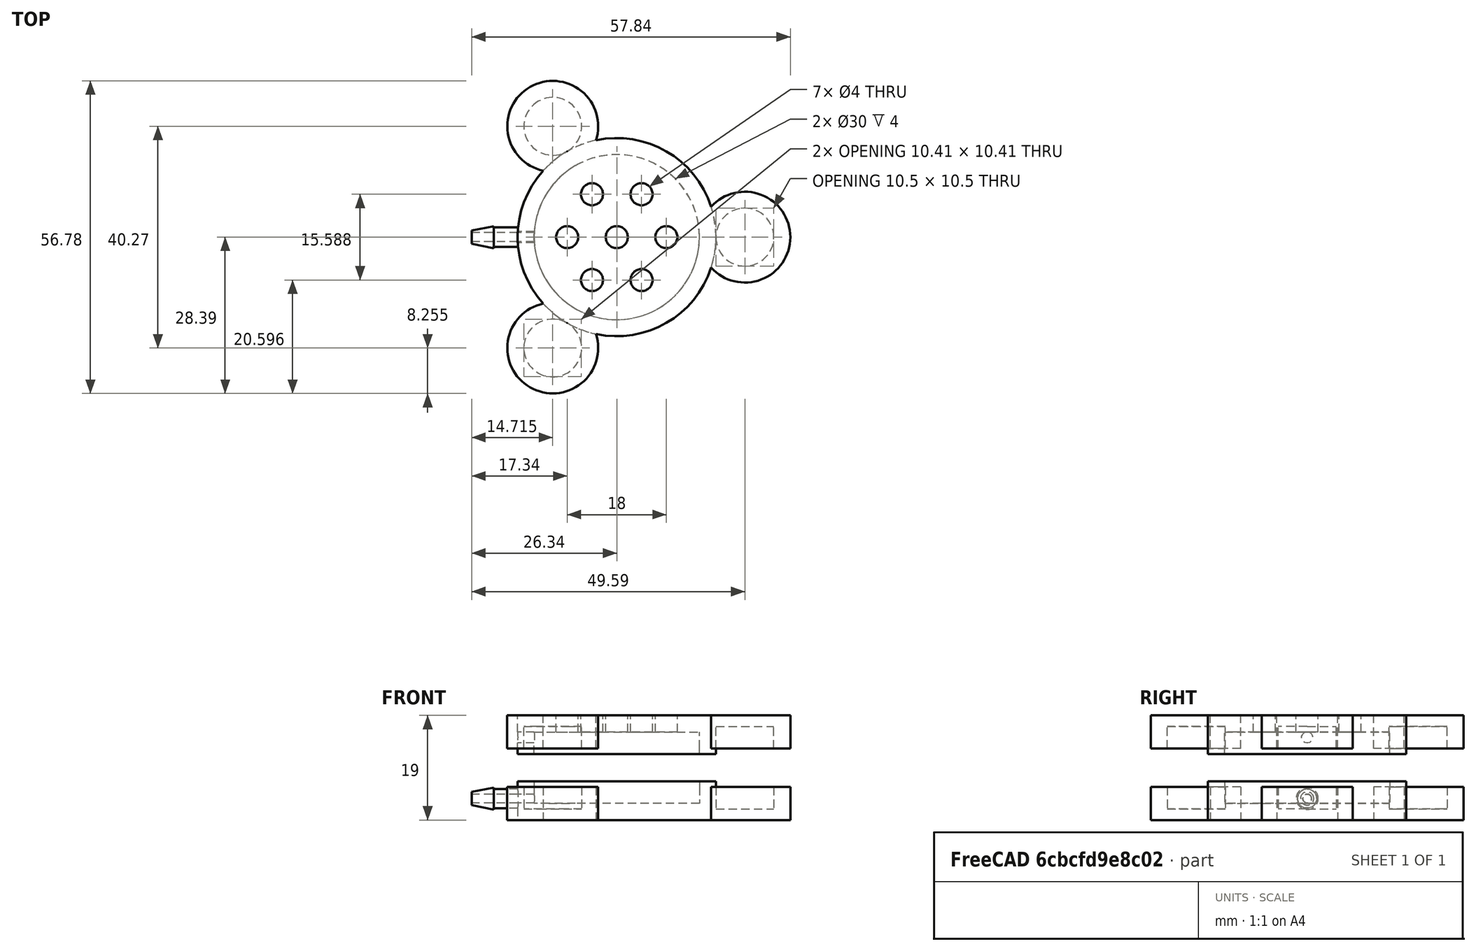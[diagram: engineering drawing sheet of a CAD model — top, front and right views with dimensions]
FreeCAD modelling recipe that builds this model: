
FCSTD DOCUMENT  (FreeCAD 0.18R4 (GitTag))
Label: PAPRtools-PortacountMaterialTestAdapter
License: All rights reserved
LicenseURL: http://en.wikipedia.org/wiki/All_rights_reserved
objects: Part::Cylinder×13, Part::Cut×6, Part::FeaturePython×4, Part::MultiFuse×4, Part::Cone×2, Part::Mirroring×1
note: 30 computed .brp shape members not serialized (recipe doc carries the construction recipe); baked Part::Feature solids carry a one-line shape summary decoded from their .brp

FEATURE [Part::Cylinder] Cylinder
  Angle = 360
  AttacherType = Attacher::AttachEngine3D
  Height = 7
  Radius = 18
FEATURE [Part::Cylinder] Cylinder001
  Angle = 360
  AttacherType = Attacher::AttachEngine3D
  Height = 4
  Radius = 15
FEATURE [Part::Cut] Cut
  Base = -> Cylinder
  Tool = -> Cylinder001
FEATURE [Part::Cylinder] Cylinder002
  Angle = 360
  AttacherType = Attacher::AttachEngine3D
  Height = 4
  Radius = 5.25
FEATURE [Part::Cylinder] Cylinder003
  Angle = 360
  AttacherType = Attacher::AttachEngine3D
  Height = 6
  Radius = 8.25
FEATURE [Part::Cut] Cut001
  Base = -> Cylinder003
  Placement = pos=(23.25,0,1) rot=(0,0,1;0rad)
  Tool = -> Cylinder002
FEATURE [Part::FeaturePython] Array  # Draft array (typed FeaturePython)
  Angle = 360
  ArrayType = 1
  Axis = (0,0,1)
  Base = -> Cut001
  Center = (0,0,0)
  Fuse = false
  IntervalAxis = (0,0,0)
  IntervalX = (1,0,0)
  IntervalY = (0,1,0)
  IntervalZ = (0,0,1)
  NumberPolar = 3
  NumberX = 1
  NumberY = 1
  NumberZ = 1
FEATURE [Part::MultiFuse] Fusion  label="Base"
  Shapes = -> [Array,Cut]
FEATURE [Part::Cylinder] Cylinder004
  Angle = 360
  AttacherType = Attacher::AttachEngine3D
  Height = 4
  Radius = 15
FEATURE [Part::Cylinder] Cylinder005
  Angle = 360
  AttacherType = Attacher::AttachEngine3D
  Height = 4
  Radius = 5.25
FEATURE [Part::Cylinder] Cylinder006
  Angle = 360
  AttacherType = Attacher::AttachEngine3D
  Height = 6
  Radius = 8.25
FEATURE [Part::Cylinder] Cylinder007
  Angle = 360
  AttacherType = Attacher::AttachEngine3D
  Height = 7
  Radius = 18
FEATURE [Part::Cut] Cut002
  Base = -> Cylinder006
  Placement = pos=(23.25,0,0) rot=(0,0,1;0rad)
  Tool = -> Cylinder005
FEATURE [Part::FeaturePython] Array001  # Draft array (typed FeaturePython)
  Angle = 360
  ArrayType = 1
  Axis = (0,0,1)
  Base = -> Cut002
  Center = (0,0,0)
  Fuse = false
  IntervalAxis = (0,0,0)
  IntervalX = (1,0,0)
  IntervalY = (0,1,0)
  IntervalZ = (0,0,1)
  NumberPolar = 3
  NumberX = 1
  NumberY = 1
  NumberZ = 1
  Placement = pos=(0,0,1) rot=(0,0,1;0rad)
FEATURE [Part::Cut] Cut003
  Base = -> Cylinder007
  Tool = -> Cylinder004
FEATURE [Part::MultiFuse] Fusion001  label="Base001"
  Shapes = -> [Array001,Cut003]
FEATURE [Part::Mirroring] Part__Mirroring  label="Base001 (Mirror #1)"
  Base = (0,0,0)
  Normal = (0,0,1)
  Placement = pos=(0,0,-5) rot=(0,0,1;0rad)
  Source = -> Fusion001
FEATURE [Part::Cylinder] Cylinder008
  Angle = 360
  AttacherType = Attacher::AttachEngine3D
  Height = 10
  Placement = pos=(9,0,0) rot=(0,0,1;0rad)
  Radius = 2
FEATURE [Part::FeaturePython] Array002  # Draft array (typed FeaturePython)
  Angle = 360
  ArrayType = 1
  Axis = (0,0,1)
  Base = -> Cylinder008
  Center = (0,0,0)
  Fuse = false
  IntervalAxis = (0,0,0)
  IntervalX = (1,0,0)
  IntervalY = (0,1,0)
  IntervalZ = (0,0,1)
  NumberPolar = 6
  NumberX = 2
  NumberY = 2
  NumberZ = 1
FEATURE [Part::Cylinder] Cylinder009
  Angle = 360
  AttacherType = Attacher::AttachEngine3D
  Height = 10
  Radius = 2
FEATURE [Part::Cylinder] Cylinder033  label="nSampleBarb"
  Angle = 360
  AttacherType = Attacher::AttachEngine3D
  Height = 18
  Radius = 0.8
FEATURE [Part::Cylinder] Cylinder034  label="pSampleBarb-Body"
  Angle = 360
  AttacherType = Attacher::AttachEngine3D
  Height = 10
  Placement = pos=(0,0,4) rot=(0,0,1;0rad)
  Radius = 1.75
FEATURE [Part::Cone] Cone  label="pSampleBarb-Bottom"
  Angle = 360
  AttacherType = Attacher::AttachEngine3D
  Height = 4
  Radius1 = 1.2
  Radius2 = 2
FEATURE [Part::Cone] Cone001  label="pSampleBarb-Top"
  Angle = 360
  AttacherType = Attacher::AttachEngine3D
  Height = 4
  Placement = pos=(0,0,14) rot=(0,0,1;0rad)
  Radius1 = 2
  Radius2 = 1.2
FEATURE [Part::MultiFuse] Fusion026  label="pSampleBarb"
  Shapes = -> [Cone,Cylinder034,Cone001]
FEATURE [Part::Cut] Cut005  label="SampleBarb"
  Base = -> Fusion026
  Placement = pos=(-8.34376,0,-8.09503) rot=(0,-1,0;1.5708rad)
  Tool = -> Cylinder033
FEATURE [Part::FeaturePython] Connect  label="TopLevelPart-MaterialTestSampler"  # WARN: FeaturePython — macro-defined, semantics opaque (R4)
  Objects = -> [Cut005,Part__Mirroring]
  Tolerance = 0
FEATURE [Part::Cylinder] Cylinder035  label="Cylinder010"
  Angle = 360
  AttacherType = Attacher::AttachEngine3D
  Height = 10
  Placement = pos=(-13,0,3) rot=(0,1,0;4.71239rad)
  Radius = 1
FEATURE [Part::MultiFuse] Fusion027
  Shapes = -> [Cylinder009,Array002,Cylinder035]
FEATURE [Part::Cut] Cut006  label="TopLevelPart-MaterialTestHolder"
  Base = -> Fusion
  Tool = -> Fusion027
